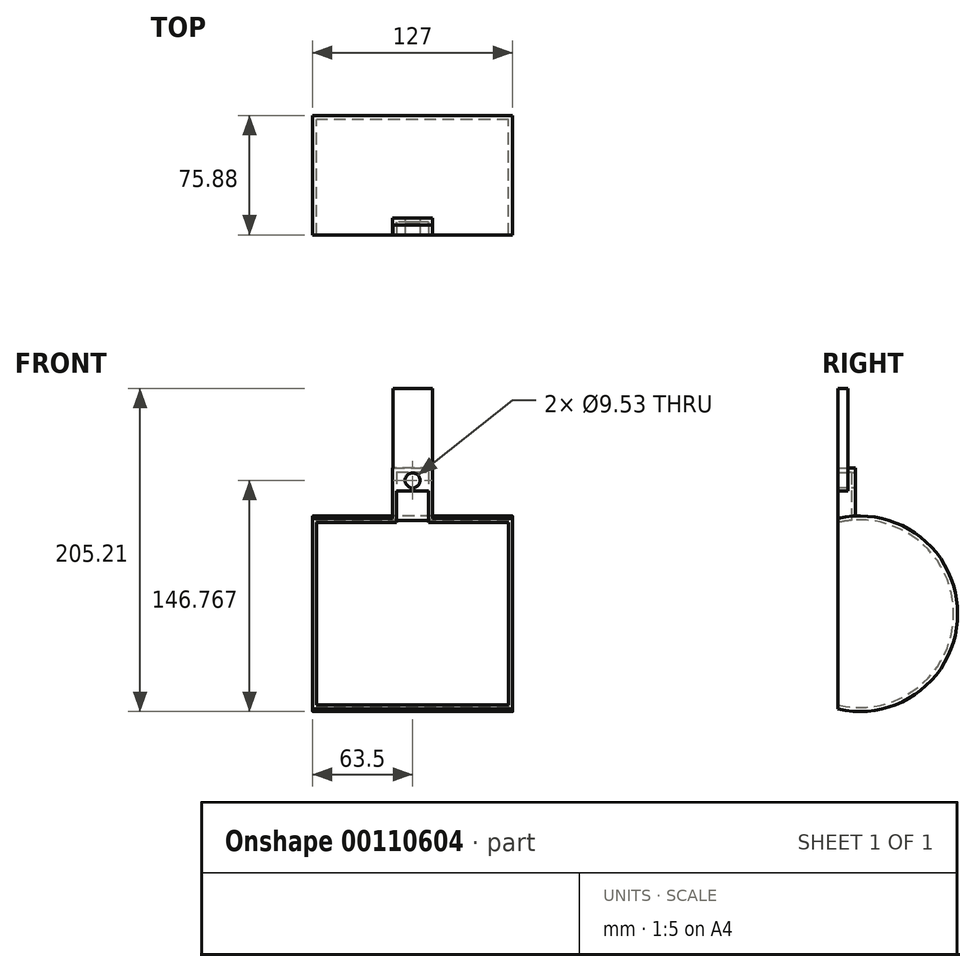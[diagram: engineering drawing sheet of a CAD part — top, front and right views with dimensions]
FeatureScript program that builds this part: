
annotation { "Feature Type Name" : "Feature", "Feature Type Description" : "" }
export const myFeature = defineFeature(function(context is Context, id is Id, definition is map)
    precondition{}
    {
        {
            var Q0;
            Q0=qCreatedBy(makeId("Right.planeOp"),FACE);
            var sketch = newSketch(context, id + "F0", { "sketchPlane" : qUnion([Q0])});
            skArc(sketch, "E0", {"start": v(0, -76.39) * mm, "mid": v(75.88, -15.85) * mm, "end": v(0, 44.69) * mm});
            skLineSegment(sketch, "E1", {"start": v(0, 44.69) * mm, "end": v(0, -76.39) * mm});
            skLineSegment(sketch, "E2", {"start": v(0, 44.69) * mm, "end": v(0, 76.57) * mm});
            skLineSegment(sketch, "E3", {"start": v(0, 76.57) * mm, "end": v(10.82, 76.57) * mm});
            skLineSegment(sketch, "E4", {"start": v(10.82, 76.57) * mm, "end": v(10.82, 46.17) * mm});
            skSolve(sketch);
        }
        {
            var Q0;
            {var subQ0=sQuery(id+"F0.wireOp",EDGE,"E1");Q0=makeQuery(id+"F0.imprint","IMPRINT",FACE,{"disambiguationData":[TD([[makeQuery(id+"F0.imprint","IMPRINT",EDGE,{"derivedFrom":subQ0}),1.0]])]});}
            extrude(context, id + "F1", {"entities" : qUnion([Q0]), "endBound" : BoundingType.SYMMETRIC, "depth" : 127 * mm});
        }
        {
            var Q0;
            {var subQ0=sQuery(id+"F0.wireOp",EDGE,"E2");Q0=makeQuery(id+"F0.imprint","IMPRINT",FACE,{"disambiguationData":[TD([[makeQuery(id+"F0.imprint","IMPRINT",EDGE,{"derivedFrom":subQ0}),-1.0]])]});}
            extrude(context, id + "F2", {"entities" : qUnion([Q0]), "operationType" : NewBodyOperationType.ADD, "endBound" : BoundingType.SYMMETRIC, "depth" : 25.4 * mm});
        }
        {
            var Q0;
            Q0=makeQuery(id+"F2.boolean.opBoolean","MERGE",FACE,{"derivedFrom":[makeQuery(id+"F1.opExtrude","SWEPT_FACE",FACE,{"disambiguationData":[OSD([sQuery(id+"F0.wireOp",EDGE,"E1")])]}),makeQuery(id+"F2.opExtrude","SWEPT_FACE",FACE,{"disambiguationData":[OSD([sQuery(id+"F0.wireOp",EDGE,"E2")])]})]});
            shell(context, id + "F3", {"entities" : qUnion([Q0]), "thickness" : 2.54 * mm});
        }
        {
            var Q0;
            Q0=qCreatedBy(makeId("Front.planeOp"),FACE);
            var sketch = newSketch(context, id + "F4", { "sketchPlane" : qUnion([Q0])});
            skLineSegment(sketch, "E5", {"start": v(0, 62.03) * mm, "end": v(-12.48, 62.03) * mm});
            skLineSegment(sketch, "E6", {"start": v(-12.48, 62.03) * mm, "end": v(-12.48, 127.27) * mm});
            skLineSegment(sketch, "E7", {"start": v(0, 62.03) * mm, "end": v(12.8, 62.03) * mm});
            skLineSegment(sketch, "E8", {"start": v(12.8, 62.03) * mm, "end": v(12.8, 127.27) * mm});
            skLineSegment(sketch, "E9", {"start": v(12.8, 127.27) * mm, "end": v(-12.48, 127.27) * mm});
            skSolve(sketch);
        }
        {
            var Q0;
            Q0 = qSketchRegion(id + "F4", true);
            extrude(context, id + "F5", {"entities" : qUnion([Q0]), "operationType" : NewBodyOperationType.ADD, "oppositeDirection" : true, "depth" : 6.35 * mm});
        }
        {
            var Q0;
            Q0=makeQuery(id+"F5.boolean.opBoolean","MERGE",FACE,{"derivedFrom":[makeQuery(id+"F2.boolean.opBoolean","MERGE",FACE,{"derivedFrom":[makeQuery(id+"F1.opExtrude","SWEPT_FACE",FACE,{"disambiguationData":[OSD([sQuery(id+"F0.wireOp",EDGE,"E1")])]}),makeQuery(id+"F2.opExtrude","SWEPT_FACE",FACE,{"disambiguationData":[OSD([sQuery(id+"F0.wireOp",EDGE,"E2")])]})]}),makeQuery(id+"F5.opExtrude","CAP_FACE",FACE,{"disambiguationData":[OSD([sQuery(id+"F4.wireOp",EDGE,"E5"),sQuery(id+"F4.wireOp",EDGE,"E6"),sQuery(id+"F4.wireOp",EDGE,"E7"),sQuery(id+"F4.wireOp",EDGE,"E8"),sQuery(id+"F4.wireOp",EDGE,"E9")])],"isStart":true})]});
            var sketch = newSketch(context, id + "F6", { "sketchPlane" : qUnion([Q0])});
            skLineSegment(sketch, "E10", {"start": v(-12.7, 68.83) * mm, "end": v(12.8, 68.83) * mm});
            skCircle(sketch, "E11", {"center": v(0, 68.83) * mm, "radius": 4.76 * mm});
            skSolve(sketch);
        }
        {
            var Q0;
            Q0 = qSketchRegion(id + "F6", true);
            extrude(context, id + "F7", {"entities" : qUnion([Q0]), "operationType" : NewBodyOperationType.REMOVE, "oppositeDirection" : true, "depth" : 25.4 * mm});
        }
    });
